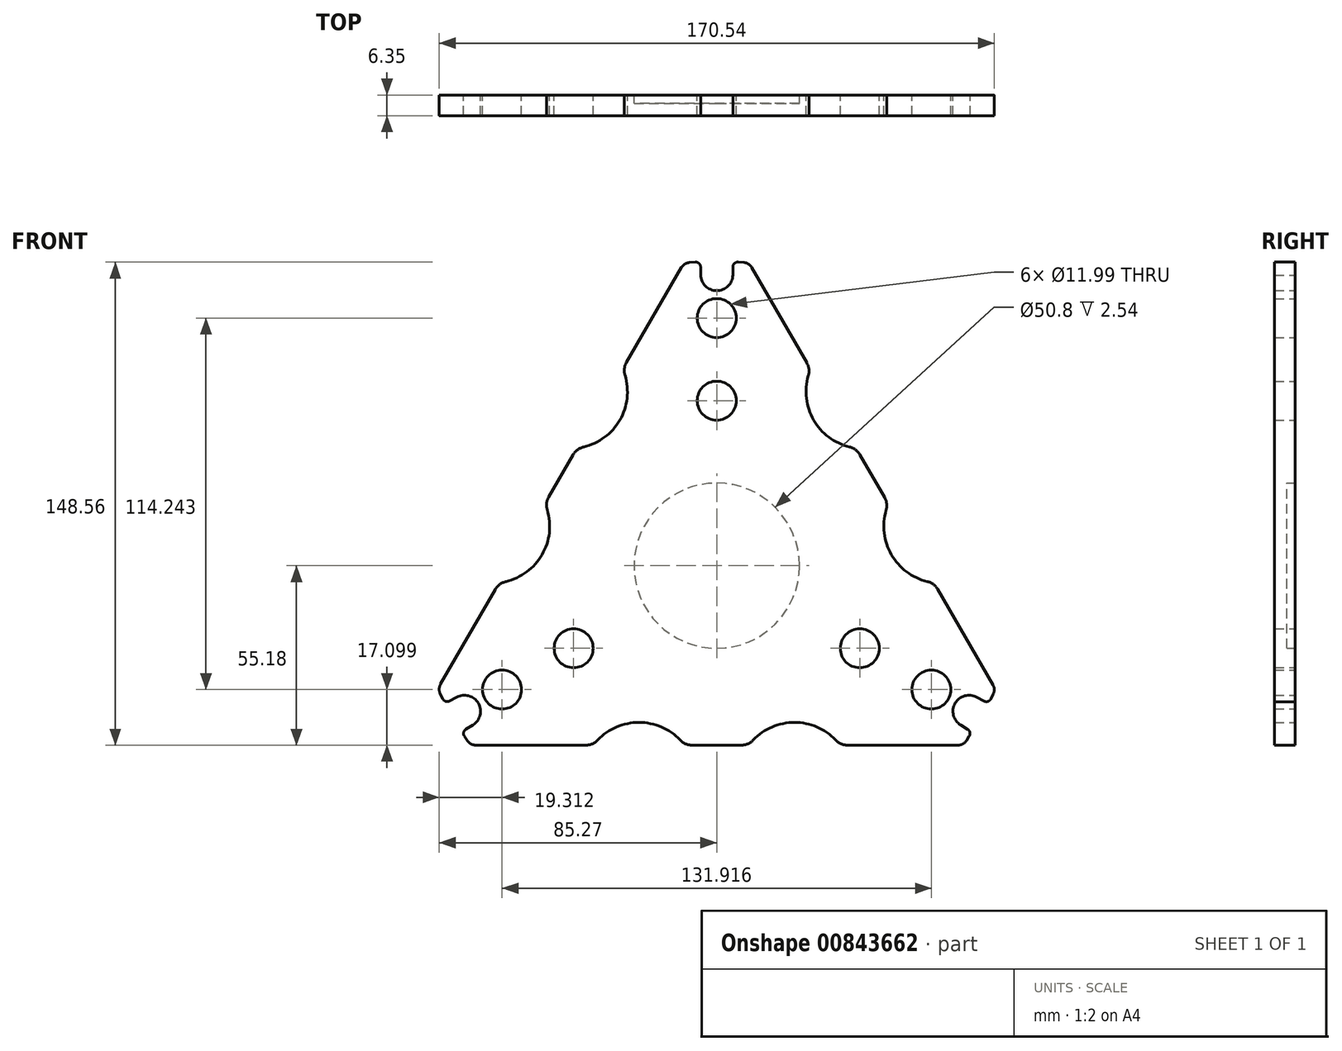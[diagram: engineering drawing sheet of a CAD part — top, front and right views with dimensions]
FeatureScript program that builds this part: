
annotation { "Feature Type Name" : "Feature", "Feature Type Description" : "" }
export const myFeature = defineFeature(function(context is Context, id is Id, definition is map)
    precondition{}
    {
        {
            var Q0;
            Q0=qCreatedBy(makeId("Front.planeOp"),FACE);
            var sketch = newSketch(context, id + "F0", { "sketchPlane" : qUnion([Q0])});
            skArc(sketch, "E0", {"start": v(85.61, -37.93) * mm, "mid": v(-81.1, 46.82) * mm, "end": v(75.65, -55.18) * mm, "construction": true});
            skCircle(sketch, "E1", {"center": v(0, 0) * mm, "radius": 76.16 * mm, "construction": true});
            skCircle(sketch, "E2", {"center": v(0, 0) * mm, "radius": 50.76 * mm, "construction": true});
            skCircle(sketch, "E3", {"center": v(0, 0) * mm, "radius": 69.85 * mm, "construction": true});
            skCircle(sketch, "E4", {"center": v(0, 0) * mm, "radius": 77.98 * mm, "construction": true});
            skCircle(sketch, "E5", {"center": v(0, 0) * mm, "radius": 89.53 * mm, "construction": true});
            skLineSegment(sketch, "E6", {"start": v(0, 0) * mm, "end": v(0, 125.8) * mm, "construction": true});
            skLineSegment(sketch, "E7", {"start": v(0, 0) * mm, "end": v(153.7, -88.74) * mm, "construction": true});
            skLineSegment(sketch, "E8", {"start": v(0, 0) * mm, "end": v(-174.19, -100.57) * mm, "construction": true});
            skArc(sketch, "E9", {"start": v(-4.95, 89.4) * mm, "mid": v(0, 84.58) * mm, "end": v(4.95, 89.4) * mm});
            skLineSegment(sketch, "E10", {"start": v(4.95, 89.4) * mm, "end": v(4.95, 93.5) * mm});
            skLineSegment(sketch, "E11", {"start": v(-4.95, 89.4) * mm, "end": v(-4.95, 93.5) * mm});
            skLineSegment(sketch, "E12", {"start": v(9.96, 93.1) * mm, "end": v(28.85, 60.39) * mm});
            skLineSegment(sketch, "E13", {"start": v(-10.07, 93.1) * mm, "end": v(-28.9, 60.5) * mm});
            skLineSegment(sketch, "E14", {"start": v(75.8, -55.18) * mm, "end": v(37.87, -55.18) * mm});
            skArc(sketch, "E15", {"start": v(79.9, -40.41) * mm, "mid": v(73.25, -42.3) * mm, "end": v(74.95, -48.99) * mm});
            skLineSegment(sketch, "E16", {"start": v(79.9, -40.41) * mm, "end": v(83.5, -42.36) * mm});
            skLineSegment(sketch, "E17", {"start": v(83.5, -42.36) * mm, "end": v(85.69, -38.06) * mm});
            skLineSegment(sketch, "E18", {"start": v(74.95, -48.99) * mm, "end": v(78.44, -51.14) * mm});
            skLineSegment(sketch, "E19", {"start": v(78.44, -51.14) * mm, "end": v(75.8, -55.18) * mm});
            skLineSegment(sketch, "E20", {"start": v(4.95, 93.5) * mm, "end": v(9.96, 93.1) * mm});
            skLineSegment(sketch, "E21", {"start": v(-4.95, 93.5) * mm, "end": v(-10.07, 93.1) * mm});
            skArc(sketch, "E22.trimOffspring", {"start": v(78.44, -51.14) * mm, "mid": v(81.1, -46.82) * mm, "end": v(83.5, -42.36) * mm, "construction": true});
            skArc(sketch, "E23", {"start": v(-74.95, -48.99) * mm, "mid": v(-73.25, -42.3) * mm, "end": v(-79.9, -40.41) * mm});
            skLineSegment(sketch, "E24", {"start": v(-74.95, -48.99) * mm, "end": v(-78.44, -51.14) * mm});
            skLineSegment(sketch, "E25", {"start": v(-79.9, -40.41) * mm, "end": v(-83.5, -42.36) * mm});
            skLineSegment(sketch, "E26", {"start": v(-83.5, -42.36) * mm, "end": v(-85.66, -37.82) * mm});
            skLineSegment(sketch, "E27", {"start": v(-78.44, -51.14) * mm, "end": v(-75.65, -55.18) * mm});
            skLineSegment(sketch, "E28.trimOffspring", {"start": v(-95.57, -55.18) * mm, "end": v(-95.68, -55.18) * mm});
            skLineSegment(sketch, "E29.trimOffspring", {"start": v(-95.68, -55.18) * mm, "end": v(-95.73, -55.27) * mm});
            skCircle(sketch, "E30", {"center": v(0, 76.16) * mm, "radius": 6 * mm});
            skCircle(sketch, "E31", {"center": v(-65.96, -38.08) * mm, "radius": 6 * mm});
            skCircle(sketch, "E32", {"center": v(65.96, -38.08) * mm, "radius": 6 * mm});
            skCircle(sketch, "E33", {"center": v(0, 50.76) * mm, "radius": 6 * mm});
            skCircle(sketch, "E34", {"center": v(43.96, -25.38) * mm, "radius": 6 * mm});
            skCircle(sketch, "E35", {"center": v(-43.96, -25.38) * mm, "radius": 6 * mm});
            skCircle(sketch, "E36", {"center": v(0, 0) * mm, "radius": 25.4 * mm});
            skLineSegment(sketch, "E37", {"start": v(0, 0) * mm, "end": v(-112.95, 134.6) * mm, "construction": true});
            skLineSegment(sketch, "E38", {"start": v(0, 0) * mm, "end": v(-212.25, 37.43) * mm, "construction": true});
            skLineSegment(sketch, "E39", {"start": v(0, 0) * mm, "end": v(44.47, -122.19) * mm, "construction": true});
            skLineSegment(sketch, "E40", {"start": v(0, 0) * mm, "end": v(-43.42, -119.3) * mm, "construction": true});
            skLineSegment(sketch, "E41", {"start": v(0, 0) * mm, "end": v(158.19, 27.9) * mm, "construction": true});
            skLineSegment(sketch, "E42", {"start": v(0, 0) * mm, "end": v(94.13, 112.18) * mm, "construction": true});
            skArc(sketch, "E43", {"start": v(60.68, 46.03) * mm, "mid": v(61.1, 47) * mm, "end": v(61.46, 47.99) * mm});
            skArc(sketch, "E44", {"start": v(52.74, 19) * mm, "mid": v(53.67, 3.4) * mm, "end": v(66.72, -5.21) * mm});
            skArc(sketch, "E45", {"start": v(-9.9, -55.18) * mm, "mid": v(-23.9, -48.18) * mm, "end": v(-37.87, -55.18) * mm});
            skArc(sketch, "E46", {"start": v(-42.95, 36.15) * mm, "mid": v(-29.78, 44.78) * mm, "end": v(-28.9, 60.5) * mm});
            skArc(sketch, "E47.trimOffspring", {"start": v(28.85, 60.39) * mm, "mid": v(29.78, 44.78) * mm, "end": v(42.83, 36.17) * mm});
            skLineSegment(sketch, "E48.trimOffspring", {"start": v(42.83, 36.17) * mm, "end": v(52.74, 19) * mm});
            skLineSegment(sketch, "E49.trimOffspring", {"start": v(66.72, -5.21) * mm, "end": v(85.69, -38.06) * mm});
            skLineSegment(sketch, "E50.trimOffspring", {"start": v(9.9, -55.18) * mm, "end": v(-9.9, -55.18) * mm});
            skArc(sketch, "E51.trimOffspring", {"start": v(37.87, -55.18) * mm, "mid": v(23.9, -48.18) * mm, "end": v(9.9, -55.18) * mm});
            skLineSegment(sketch, "E52.trimOffspring", {"start": v(-37.87, -55.18) * mm, "end": v(-75.65, -55.18) * mm});
            skLineSegment(sketch, "E53.trimOffspring", {"start": v(-66.84, -5.22) * mm, "end": v(-85.66, -37.82) * mm});
            skArc(sketch, "E54.trimOffspring", {"start": v(-66.84, -5.22) * mm, "mid": v(-53.67, 3.4) * mm, "end": v(-52.79, 19.12) * mm});
            skLineSegment(sketch, "E55.trimOffspring", {"start": v(-42.95, 36.15) * mm, "end": v(-52.79, 19.12) * mm});
            skSolve(sketch);
        }
        {
            var Q0;
            Q0 = qSketchRegion(id + "F0", true);
            var Q1;
            Q1=makeQuery(id+"F0.imprint","IMPRINT",FACE,{"disambiguationData":[TD([[makeQuery(id+"F0.imprint","IMPRINT",EDGE,{"derivedFrom":sQuery(id+"F0.wireOp",EDGE,"E36")}),1.0]])]});
            extrude(context, id + "F1", {"entities" : qUnion([Q0, Q1]), "depth" : 6.35 * mm, "offsetDistance" : 25.4 * mm});
        }
        {
            var Q0;
            Q0=makeQuery(id+"F0.imprint","IMPRINT",FACE,{"disambiguationData":[TD([[makeQuery(id+"F0.imprint","IMPRINT",EDGE,{"derivedFrom":sQuery(id+"F0.wireOp",EDGE,"E36")}),1.0]])]});
            extrude(context, id + "F2", {"entities" : qUnion([Q0]), "operationType" : NewBodyOperationType.REMOVE, "depth" : 2.54 * mm, "offsetDistance" : 25.4 * mm});
        }
        {
            var Q0;
            Q0=makeQuery(id+"F1.opExtrude","SWEPT_EDGE",EDGE,{"disambiguationData":[OSD([sQuery(id+"F0.wireOp",EDGE,"E16"),sQuery(id+"F0.wireOp",EDGE,"E17")])]});
            var Q1;
            Q1=makeQuery(id+"F1.opExtrude","SWEPT_EDGE",EDGE,{"disambiguationData":[OSD([sQuery(id+"F0.wireOp",EDGE,"E18"),sQuery(id+"F0.wireOp",EDGE,"E19")])]});
            var Q2;
            Q2=makeQuery(id+"F1.opExtrude","SWEPT_EDGE",EDGE,{"disambiguationData":[OSD([sQuery(id+"F0.wireOp",EDGE,"E10"),sQuery(id+"F0.wireOp",EDGE,"E20")])]});
            var Q3;
            Q3=makeQuery(id+"F1.opExtrude","SWEPT_EDGE",EDGE,{"disambiguationData":[OSD([sQuery(id+"F0.wireOp",EDGE,"E11"),sQuery(id+"F0.wireOp",EDGE,"E21")])]});
            var Q4;
            Q4=makeQuery(id+"F1.opExtrude","SWEPT_EDGE",EDGE,{"disambiguationData":[OSD([sQuery(id+"F0.wireOp",EDGE,"E25"),sQuery(id+"F0.wireOp",EDGE,"E26")])]});
            var Q5;
            Q5=makeQuery(id+"F1.opExtrude","SWEPT_EDGE",EDGE,{"disambiguationData":[OSD([sQuery(id+"F0.wireOp",EDGE,"E24"),sQuery(id+"F0.wireOp",EDGE,"E27")])]});
            fillet(context, id + "F3", {"entities" : qUnion([Q0, Q1, Q2, Q3, Q4, Q5]), "radius" : 1.52 * mm, "tangentPropagation" : true, "allowEdgeOverflow" : false});
        }
        {
            var Q0;
            Q0=makeQuery(id+"F1.opExtrude","SWEPT_EDGE",EDGE,{"disambiguationData":[OSD([sQuery(id+"F0.wireOp",EDGE,"E26"),sQuery(id+"F0.wireOp",EDGE,"E53.trimOffspring")])]});
            var Q1;
            Q1=makeQuery(id+"F1.opExtrude","SWEPT_EDGE",EDGE,{"disambiguationData":[OSD([sQuery(id+"F0.wireOp",EDGE,"E27"),sQuery(id+"F0.wireOp",EDGE,"E52.trimOffspring")])]});
            var Q2;
            Q2=makeQuery(id+"F1.opExtrude","SWEPT_EDGE",EDGE,{"disambiguationData":[OSD([sQuery(id+"F0.wireOp",EDGE,"E14"),sQuery(id+"F0.wireOp",EDGE,"E19")])]});
            var Q3;
            Q3=makeQuery(id+"F1.opExtrude","SWEPT_EDGE",EDGE,{"disambiguationData":[OSD([sQuery(id+"F0.wireOp",EDGE,"E17"),sQuery(id+"F0.wireOp",EDGE,"E49.trimOffspring")])]});
            var Q4;
            Q4=makeQuery(id+"F1.opExtrude","SWEPT_EDGE",EDGE,{"disambiguationData":[OSD([sQuery(id+"F0.wireOp",EDGE,"E12"),sQuery(id+"F0.wireOp",EDGE,"E20")])]});
            var Q5;
            Q5=makeQuery(id+"F1.opExtrude","SWEPT_EDGE",EDGE,{"disambiguationData":[OSD([sQuery(id+"F0.wireOp",EDGE,"E13"),sQuery(id+"F0.wireOp",EDGE,"E21")])]});
            fillet(context, id + "F4", {"entities" : qUnion([Q0, Q1, Q2, Q3, Q4, Q5]), "radius" : 3.05 * mm, "tangentPropagation" : true, "allowEdgeOverflow" : false});
        }
        {
            var Q0;
            Q0=makeQuery(id+"F1.opExtrude","SWEPT_EDGE",EDGE,{"disambiguationData":[OSD([sQuery(id+"F0.wireOp",EDGE,"E12"),sQuery(id+"F0.wireOp",EDGE,"E47.trimOffspring")])]});
            var Q1;
            Q1=makeQuery(id+"F1.opExtrude","SWEPT_EDGE",EDGE,{"disambiguationData":[OSD([sQuery(id+"F0.wireOp",EDGE,"E47.trimOffspring"),sQuery(id+"F0.wireOp",EDGE,"E48.trimOffspring")])]});
            var Q2;
            Q2=makeQuery(id+"F1.opExtrude","SWEPT_EDGE",EDGE,{"disambiguationData":[OSD([sQuery(id+"F0.wireOp",EDGE,"E44"),sQuery(id+"F0.wireOp",EDGE,"E48.trimOffspring")])]});
            var Q3;
            Q3=makeQuery(id+"F1.opExtrude","SWEPT_EDGE",EDGE,{"disambiguationData":[OSD([sQuery(id+"F0.wireOp",EDGE,"E44"),sQuery(id+"F0.wireOp",EDGE,"E49.trimOffspring")])]});
            var Q4;
            Q4=makeQuery(id+"F1.opExtrude","SWEPT_EDGE",EDGE,{"disambiguationData":[OSD([sQuery(id+"F0.wireOp",EDGE,"E14"),sQuery(id+"F0.wireOp",EDGE,"E51.trimOffspring")])]});
            var Q5;
            Q5=makeQuery(id+"F1.opExtrude","SWEPT_EDGE",EDGE,{"disambiguationData":[OSD([sQuery(id+"F0.wireOp",EDGE,"E50.trimOffspring"),sQuery(id+"F0.wireOp",EDGE,"E51.trimOffspring")])]});
            var Q6;
            Q6=makeQuery(id+"F1.opExtrude","SWEPT_EDGE",EDGE,{"disambiguationData":[OSD([sQuery(id+"F0.wireOp",EDGE,"E45"),sQuery(id+"F0.wireOp",EDGE,"E50.trimOffspring")])]});
            var Q7;
            Q7=makeQuery(id+"F1.opExtrude","SWEPT_EDGE",EDGE,{"disambiguationData":[OSD([sQuery(id+"F0.wireOp",EDGE,"E45"),sQuery(id+"F0.wireOp",EDGE,"E52.trimOffspring")])]});
            var Q8;
            Q8=makeQuery(id+"F1.opExtrude","SWEPT_EDGE",EDGE,{"disambiguationData":[OSD([sQuery(id+"F0.wireOp",EDGE,"E53.trimOffspring"),sQuery(id+"F0.wireOp",EDGE,"E54.trimOffspring")])]});
            var Q9;
            Q9=makeQuery(id+"F1.opExtrude","SWEPT_EDGE",EDGE,{"disambiguationData":[OSD([sQuery(id+"F0.wireOp",EDGE,"E54.trimOffspring"),sQuery(id+"F0.wireOp",EDGE,"E55.trimOffspring")])]});
            var Q10;
            Q10=makeQuery(id+"F1.opExtrude","SWEPT_EDGE",EDGE,{"disambiguationData":[OSD([sQuery(id+"F0.wireOp",EDGE,"E46"),sQuery(id+"F0.wireOp",EDGE,"E55.trimOffspring")])]});
            var Q11;
            Q11=makeQuery(id+"F1.opExtrude","SWEPT_EDGE",EDGE,{"disambiguationData":[OSD([sQuery(id+"F0.wireOp",EDGE,"E13"),sQuery(id+"F0.wireOp",EDGE,"E46")])]});
            fillet(context, id + "F5", {"entities" : qUnion([Q0, Q1, Q2, Q3, Q4, Q5, Q6, Q7, Q8, Q9, Q10, Q11]), "radius" : 5.08 * mm, "tangentPropagation" : true, "allowEdgeOverflow" : false});
        }
    });
